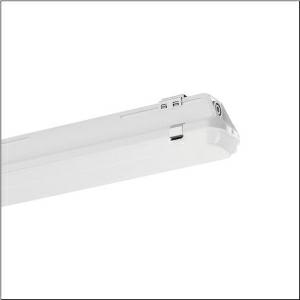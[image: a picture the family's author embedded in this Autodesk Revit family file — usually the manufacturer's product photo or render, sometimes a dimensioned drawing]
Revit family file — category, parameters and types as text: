
# Revit family: monsun_r__21_emergency_51fb20dp467b3h_0bb8
name_source: partatom
category: Lighting Fixtures
units: mm (PartAtom-declared; Revit-internal decimal feet)

## family parameters
Cut with Voids When Loaded = No
Host = Face
Light Source = No
Part Type = Normal
Room Calculation Point = No
Round Connector Dimension = Use Diameter
Shared = No

## types (1)
- --- (1 x LED, 5460 lm, 42.2 W, 4000K)
    Apparent Load = 42 VA
    CIE Flux Codes = 45 75 93 94 100
    Color Rendering = 80
    Color Temperature = 4000K
    Default Elevation = 1800 mm
    Description = Monsun® 21 emergency, damp-proof luminaire, chain hanger, primary optical cover: enclosure, of PC, light emission: direct distribution, primary light characteristic: symmetric, installation type: vertical mounting, horizontal mounting, surface-mounted, suspended mounting, LED, rated luminous flux: 5.460lm, luminous efficacy: 129lm/W, light colour: 840, colour temperature: 4000K, control gear: ECG DALI, with terminal, 5+3-pole, max. 2.5mm², mains connection: 220..240V, AC, 50/60Hz, rated input power: 42W, control gear: single battery element, battery: NiCd, 4,5Ah, mains connection: 230V, housing, of glass-fibre reinforced polyester, uncoated, bright grey, length: 1.590mm, width: 90mm, height: 88mm, clip for enclosure, of stainless steel (V2A), ceiling mounting element, of stainless steel (V2A), chain hanger, of stainless steel (V2A), protection rating (complete): IP66, insulation class (complete): insulation class I (protective earthing), certification: CE, UKCA, protection symbol: D, impact resistance: IK08, permissible operating ambient temperature: +5..+25°C, standard: EN 60598-2-1, EN 50419, EN 60598-2-22, corresponds to IFS (International Featured Standards) requirements for safety and quality in the food industry, for indoor or canopied outdoor use, no direct snow, no direct sun, no direct rain, packaging unit: 1 piece
    Height = 89 mm
    Lamp = 1 x LED
    Lamp Light Flux = 5460 lm
    Lamp Power = 42.2 W
    Lamp count = 1
    Length = 1590 mm
    Luminous efficacy = 129 lm/W
    Manufacturer = Siteco
    ModVariant = No
    Model = 51FB20DP467B3H
    Mounting Place = Ceiling
    Mounting Type = Pendant
    Number of Poles = 1
    OnlyDefault = Yes
    Power Factor = 1
    Product Name = Monsun® 21 emergency
    Product group = damp-proof luminaire | ceiling pendant
    ProductGroupID = 908
    Protection Class = Protection class I
    Protection Degree = IP 66
    RLX_Detail_Level = 1
    RlxData = <blob elided: 92041 chars, md5=56601952>
    Socket = socket
    Standby Power = 0 W
    System Light Flux = 5460 lm
    System Power = 42 W
    Type Comments = factory setting: luminous flux: 100 % | dim-lin: 254 | 261 mA
    Type Image = l_1006717.jpg
    URL = http://relux.com
    VarID = @adj_124783
    Voltage = 0 V
    Weight = 0.00 kg
    Width = 90 mm

## geometry (parser evidence)
native form markers: Blend x4, Sweep x12
no freeform markers — native parametric forms only
